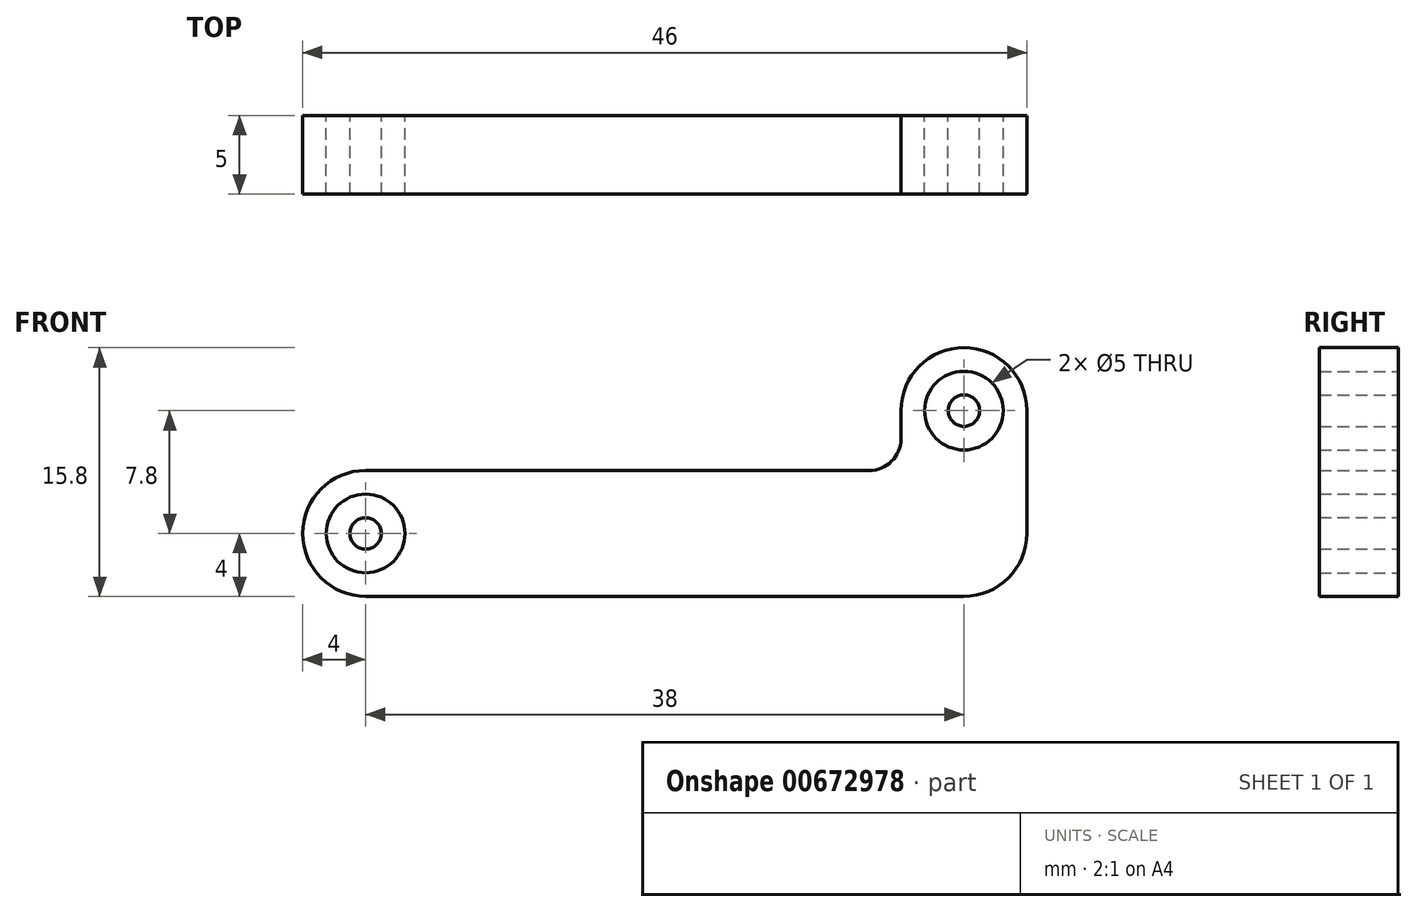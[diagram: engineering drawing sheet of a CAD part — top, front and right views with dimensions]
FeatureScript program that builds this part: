
annotation { "Feature Type Name" : "Feature", "Feature Type Description" : "" }
export const myFeature = defineFeature(function(context is Context, id is Id, definition is map)
    precondition{}
    {
        {
            var Q0;
            Q0=qCreatedBy(makeId("Front.planeOp"),FACE);
            var sketch = newSketch(context, id + "F0", { "sketchPlane" : qUnion([Q0])});
            skCircle(sketch, "E0", {"center": v(0, 0) * mm, "radius": 4 * mm});
            skCircle(sketch, "E1", {"center": v(0, 0) * mm, "radius": 2.5 * mm});
            skCircle(sketch, "E2", {"center": v(0, 0) * mm, "radius": 1 * mm});
            skCircle(sketch, "E3", {"center": v(38, 7.8) * mm, "radius": 4 * mm});
            skCircle(sketch, "E4", {"center": v(38, 7.8) * mm, "radius": 2.5 * mm});
            skCircle(sketch, "E5", {"center": v(38, 7.8) * mm, "radius": 1 * mm});
            skLineSegment(sketch, "E6", {"start": v(0, 4) * mm, "end": v(32, 4) * mm});
            skLineSegment(sketch, "E7", {"start": v(34, 7.8) * mm, "end": v(34, 6) * mm});
            skLineSegment(sketch, "E8", {"start": v(42, 7.8) * mm, "end": v(42, 0) * mm});
            skLineSegment(sketch, "E9", {"start": v(0, -4) * mm, "end": v(38, -4) * mm});
            skPoint(sketch, "E10.orphan", {"position": v(38, 4) * mm});
            skPoint(sketch, "E11.visualSharp", {"position": v(34, 4) * mm});
            skArc(sketch, "E11.filletArc", {"start": v(32, 4) * mm, "mid": v(33.41, 4.59) * mm, "end": v(34, 6) * mm});
            skPoint(sketch, "E12.visualSharp", {"position": v(42, -4) * mm});
            skArc(sketch, "E12.filletArc", {"start": v(38, -4) * mm, "mid": v(40.83, -2.83) * mm, "end": v(42, 0) * mm});
            skSolve(sketch);
        }
        {
            var Q0;
            Q0 = qSketchRegion(id + "F0", true);
            var Q1;
            Q1=makeQuery(id+"F0.imprint","IMPRINT",FACE,{"disambiguationData":[TD([[makeQuery(id+"F0.imprint","IMPRINT",EDGE,{"derivedFrom":sQuery(id+"F0.wireOp",EDGE,"E2")}),1.0]])]});
            var Q2;
            Q2=makeQuery(id+"F0.imprint","IMPRINT",FACE,{"disambiguationData":[TD([[makeQuery(id+"F0.imprint","IMPRINT",EDGE,{"derivedFrom":sQuery(id+"F0.wireOp",EDGE,"E5")}),1.0]])]});
            extrude(context, id + "F1", {"entities" : qUnion([Q0, Q1, Q2]), "depth" : 5 * mm, "offsetDistance" : 25 * mm});
        }
    });
